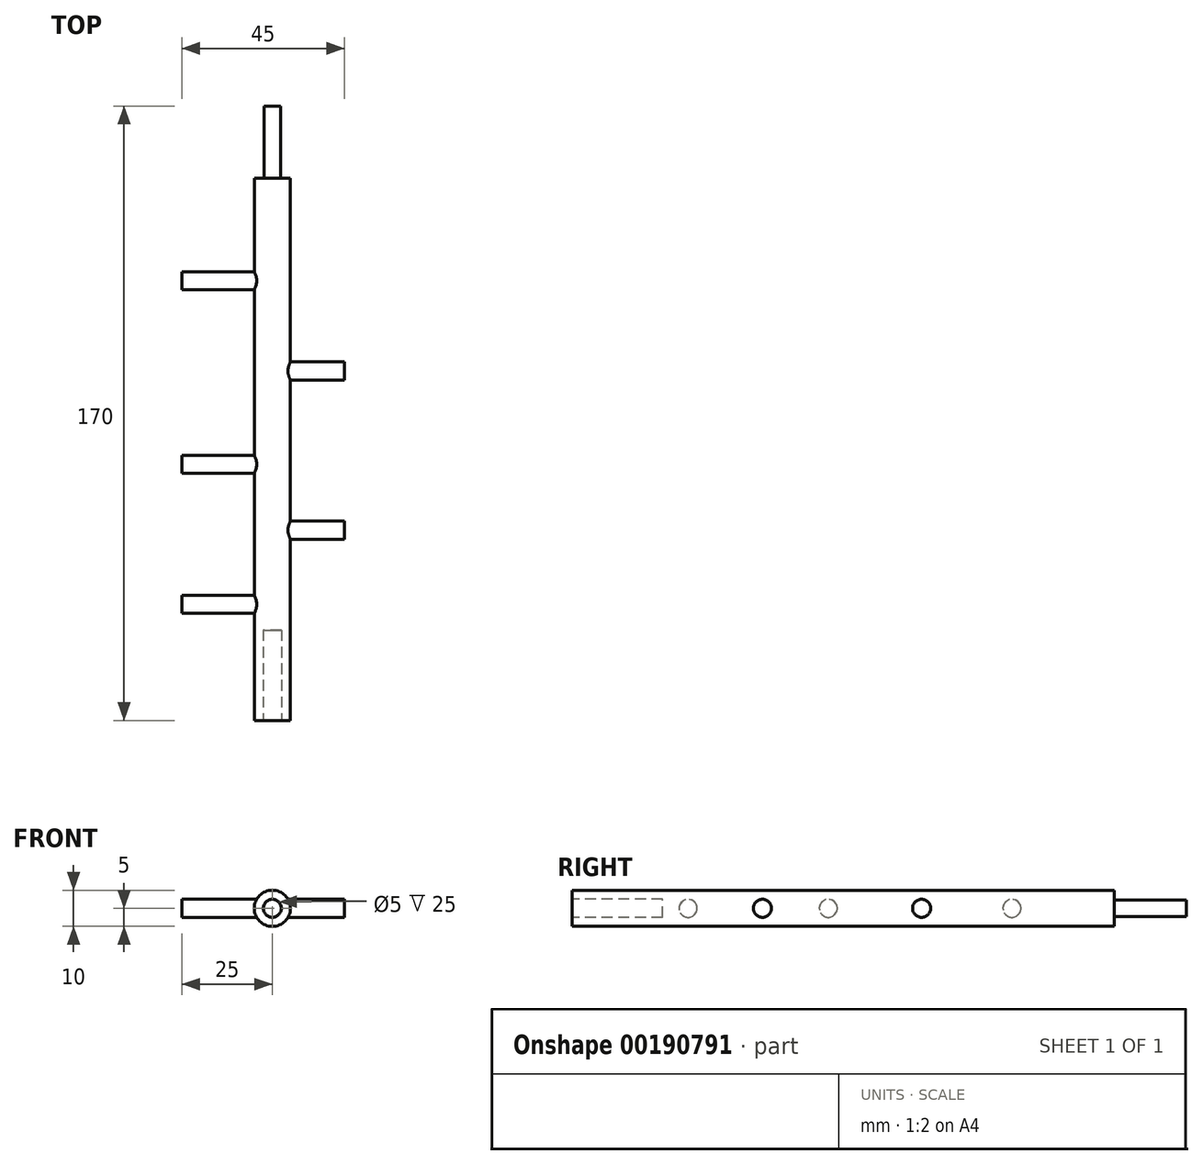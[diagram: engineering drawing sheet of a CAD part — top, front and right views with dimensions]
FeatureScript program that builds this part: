
annotation { "Feature Type Name" : "Feature", "Feature Type Description" : "" }
export const myFeature = defineFeature(function(context is Context, id is Id, definition is map)
    precondition{}
    {
        {
            var Q0;
            Q0=qCreatedBy(makeId("Front.planeOp"),FACE);
            var sketch = newSketch(context, id + "F0", { "sketchPlane" : qUnion([Q0])});
            skCircle(sketch, "E0", {"center": v(0, 0) * mm, "radius": 5 * mm});
            skSolve(sketch);
        }
        {
            var Q0;
            Q0 = qSketchRegion(id + "F0", true);
            extrude(context, id + "F1", {"entities" : qUnion([Q0]), "depth" : 150 * mm, "symmetric" : true});
        }
        {
            var Q0;
            Q0=makeQuery(id+"F1.opExtrude","CAP_FACE",FACE,{"disambiguationData":[OSD([sQuery(id+"F0.wireOp",EDGE,"E0")])],"isStart":false});
            var sketch = newSketch(context, id + "F2", { "sketchPlane" : qUnion([Q0])});
            skCircle(sketch, "E1", {"center": v(0, 0) * mm, "radius": 2.5 * mm});
            skSolve(sketch);
        }
        {
            var Q0;
            Q0 = qSketchRegion(id + "F2", true);
            extrude(context, id + "F3", {"entities" : qUnion([Q0]), "operationType" : NewBodyOperationType.REMOVE, "oppositeDirection" : true, "depth" : 25 * mm});
        }
        {
            var Q0;
            Q0=qCreatedBy(makeId("Right.planeOp"),FACE);
            var sketch = newSketch(context, id + "F4", { "sketchPlane" : qUnion([Q0])});
            skCircle(sketch, "E2", {"center": v(21.7, 0) * mm, "radius": 2.5 * mm});
            skCircle(sketch, "E3", {"center": v(-22.34, 0) * mm, "radius": 2.5 * mm});
            skSolve(sketch);
        }
        {
            var Q0;
            Q0 = qSketchRegion(id + "F4", true);
            extrude(context, id + "F5", {"entities" : qUnion([Q0]), "operationType" : NewBodyOperationType.ADD, "depth" : 20 * mm});
        }
        {
            var Q0;
            Q0=makeQuery(id+"F1.opExtrude","CAP_FACE",FACE,{"disambiguationData":[OSD([sQuery(id+"F0.wireOp",EDGE,"E0")])],"isStart":true});
            var sketch = newSketch(context, id + "F6", { "sketchPlane" : qUnion([Q0])});
            skCircle(sketch, "E4", {"center": v(0, 0) * mm, "radius": 2.25 * mm});
            skSolve(sketch);
        }
        {
            var Q0;
            Q0 = qSketchRegion(id + "F6", true);
            extrude(context, id + "F7", {"entities" : qUnion([Q0]), "operationType" : NewBodyOperationType.ADD, "depth" : 20 * mm});
        }
        {
            var Q0;
            Q0=qCreatedBy(makeId("Right.planeOp"),FACE);
            var sketch = newSketch(context, id + "F8", { "sketchPlane" : qUnion([Q0])});
            skCircle(sketch, "E5", {"center": v(46.7, 0) * mm, "radius": 2.5 * mm});
            skCircle(sketch, "E6", {"center": v(-4.1, 0) * mm, "radius": 2.5 * mm});
            skCircle(sketch, "E7", {"center": v(-42.9, 0) * mm, "radius": 2.5 * mm});
            skSolve(sketch);
        }
        {
            var Q0;
            Q0 = qSketchRegion(id + "F8", true);
            extrude(context, id + "F9", {"entities" : qUnion([Q0]), "operationType" : NewBodyOperationType.ADD, "oppositeDirection" : true, "depth" : 25 * mm});
        }
    });
